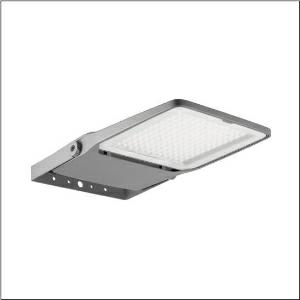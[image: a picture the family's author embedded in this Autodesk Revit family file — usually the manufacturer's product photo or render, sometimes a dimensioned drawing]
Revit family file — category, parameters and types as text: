
# Revit family: floodlight_fl_20_midi___pl43_5xa7682d1a2ac_194d
name_source: partatom
category: Lighting Fixtures
units: mm (PartAtom-declared; Revit-internal decimal feet)

## family parameters
Cut with Voids When Loaded = No
Host = Face
Light Source = No
Part Type = Normal
Room Calculation Point = No
Round Connector Dimension = Use Diameter
Shared = No

## types (1)
- --- (1 x LED 3000K / CRI = 80 (unbekannt), 14980 lm, 3000K)
    Apparent Load = 142 VA
    CIE Flux Codes = 32 74 99 100 100
    Color Rendering = 80
    Color Temperature = 3000K
    Default Elevation = 1800 mm
    Description = Floodlight FL 20 midi, floodlight, primary light control with lens, of plastic, primary optical cover: protective disc, of toughened safety glass, transparent, light distribution: PL43, light emission: direct distribution, primary light characteristic: asymmetric, installation type: surface-mounted, LED High Power LED, rated luminous flux: 14.980 lm, light colour: 830, colour temperature: 3000K, control gear: ECG Plus, control: flexible luminous flux parameterisation, time-dependent luminous flux control, digital communication interface, power reduction, overheat protection, electronic power reduction, with terminal, 5-pole, max. 2.5mm², mains connection: 220..240V, AC, 50/60Hz, rated input power: 142W, LED unit, of diecast aluminium, powder-coated, Siteco® metallic grey (DB 702S), length: 731 mm, width: 450 mm, height: 76mm, housing frame, of diecast aluminium, powder-coated, Siteco® metallic grey (DB 702S), wall fastening, of steel, powder-coated, Siteco® metallic grey (DB 702S), DALIprotection rating (complete): IP66, insulation class (complete): insulation class II (safety insulation), certification: CE, ENEC, VDE, protection symbol: D, permissible ambient temperature for indoor applications: -40..+40°C, permissible ambient temperature for outdoor applications: -40..+50°C, standard: DIN EN 12944, packaging unit: 1 piece

Light Distribution: PL43
    Height = 76 mm
    Lamp = 1 x LED 3000K / CRI >= 80 (unbekannt)
    Lamp Light Flux = 14980 lm
    Lamp count = 1
    Length = 731 mm
    Luminous efficacy = 105 lm/W
    Manufacturer = Siteco
    ModVariant = No
    Model = 5XA7682D1A2AC
    Number of Poles = 1
    OnlyDefault = Yes
    Power Factor = 1
    Product Name = Floodlight FL 20 midi | PL43
    Product group = floodlight | pylon top
    ProductGroupID = 6101
    Protection Class = Protection class II
    Protection Degree = IP 66
    RLX_Detail_Level = 1
    RlxData = <blob elided: 91901 chars, md5=52230046>
    Socket = socket
    Standby Power = 0 W
    System Light Flux = 14980 lm
    System Power = 142 W
    Type Comments = factory setting: luminous flux: 100 % | dim-lin: 254 | 489 mA
    Type Image = l_1005944.jpg
    URL = http://relux.com
    VarID = @adj_144057
    Voltage = 0 V
    Weight = 0.00 kg
    Width = 450 mm

## geometry (parser evidence)
native form markers: Blend x4, Sweep x12
no freeform markers — native parametric forms only
